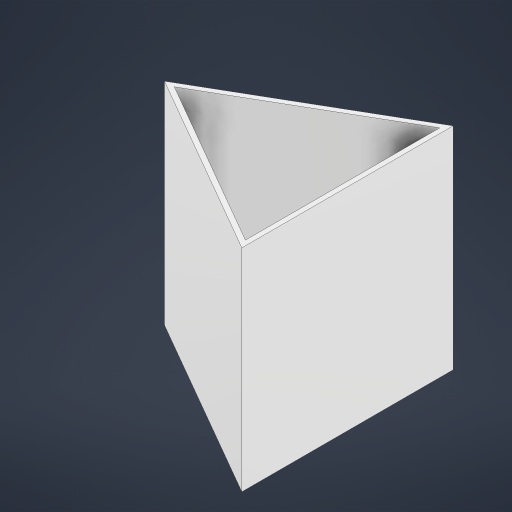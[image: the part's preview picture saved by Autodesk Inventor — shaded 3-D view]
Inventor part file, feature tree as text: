
AUTODESK INVENTOR PART (.ipt)
format: ipt  version: 2023 (Build 270158000, 158)  size: 170,496 bytes
history: native  units: mm
features: extrude x1, sketch x1
ambient origin geometry x8: Origin, YZ Plane, XZ Plane, XY Plane, X Axis, Y Axis, Z Axis, Center Point
bodies: Body1 (feature_tree)
feature tree (2):
  extrude  "Extrusion5"  Depth=54.0mm
  sketch  "Sketch2"  dims[d2=2.0mm d15=10.0mm d24=54.0mm d25=5.0mm d32=1.25mm d35=54.0mm d36=0.0mm]
